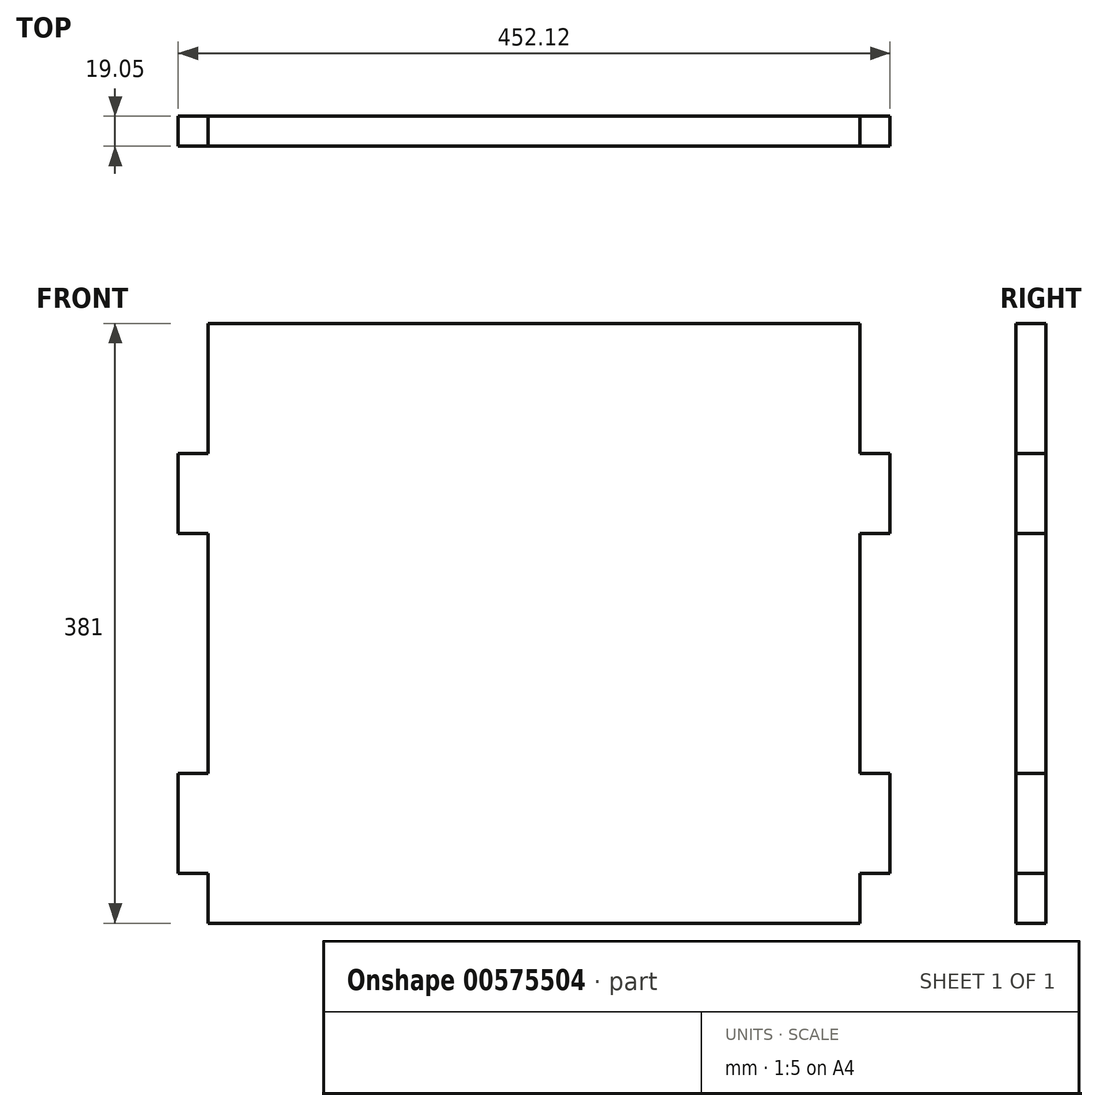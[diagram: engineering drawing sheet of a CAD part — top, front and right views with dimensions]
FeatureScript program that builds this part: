
annotation { "Feature Type Name" : "Feature", "Feature Type Description" : "" }
export const myFeature = defineFeature(function(context is Context, id is Id, definition is map)
    precondition{}
    {
        {
            var Q0;
            Q0=qCreatedBy(makeId("Front.planeOp"),FACE);
            var sketch = newSketch(context, id + "F0", { "sketchPlane" : qUnion([Q0])});
            skLineSegment(sketch, "E0.bottom", {"start": v(-259.22, 192.57) * mm, "end": v(154.8, 192.57) * mm});
            skLineSegment(sketch, "E0.top", {"start": v(-259.22, -188.43) * mm, "end": v(154.8, -188.43) * mm});
            skLineSegment(sketch, "E0.left", {"start": v(-259.22, 192.57) * mm, "end": v(-259.22, -188.43) * mm});
            skLineSegment(sketch, "E0.right", {"start": v(154.8, 192.57) * mm, "end": v(154.8, -188.43) * mm});
            skLineSegment(sketch, "E1", {"start": v(-259.22, -188.43) * mm, "end": v(-259.22, -156.68) * mm});
            skLineSegment(sketch, "E2.bottom", {"start": v(-259.22, -156.68) * mm, "end": v(-278.27, -156.68) * mm});
            skLineSegment(sketch, "E2.top", {"start": v(-259.22, -93.18) * mm, "end": v(-278.27, -93.18) * mm});
            skLineSegment(sketch, "E2.left", {"start": v(-259.22, -156.68) * mm, "end": v(-259.22, -93.18) * mm});
            skLineSegment(sketch, "E2.right", {"start": v(-278.27, -156.68) * mm, "end": v(-278.27, -93.18) * mm});
            skLineSegment(sketch, "E3", {"start": v(-278.27, -93.18) * mm, "end": v(-278.27, 59.22) * mm});
            skLineSegment(sketch, "E4.bottom", {"start": v(-278.27, 59.22) * mm, "end": v(-259.22, 59.22) * mm});
            skLineSegment(sketch, "E4.top", {"start": v(-278.27, 110.02) * mm, "end": v(-259.22, 110.02) * mm});
            skLineSegment(sketch, "E4.left", {"start": v(-278.27, 59.22) * mm, "end": v(-278.27, 110.02) * mm});
            skLineSegment(sketch, "E4.right", {"start": v(-259.22, 59.22) * mm, "end": v(-259.22, 110.02) * mm});
            skLineSegment(sketch, "E5", {"start": v(-259.22, 192.57) * mm, "end": v(-52.2, 192.57) * mm});
            skLineSegment(sketch, "E6", {"start": v(-52.2, 192.57) * mm, "end": v(-52.2, 169.4) * mm});
            skLineSegment(sketch, "E7.MirrorCS", {"start": v(154.8, -93.18) * mm, "end": v(173.85, -93.18) * mm});
            skLineSegment(sketch, "E8.MirrorCS", {"start": v(154.8, -156.68) * mm, "end": v(173.85, -156.68) * mm});
            skLineSegment(sketch, "E9.MirrorCS", {"start": v(173.85, 110.02) * mm, "end": v(154.8, 110.02) * mm});
            skLineSegment(sketch, "E10.MirrorCS", {"start": v(173.85, 59.22) * mm, "end": v(154.8, 59.22) * mm});
            skLineSegment(sketch, "E11.MirrorCS", {"start": v(173.85, -156.68) * mm, "end": v(173.85, -93.18) * mm});
            skLineSegment(sketch, "E12.MirrorCS", {"start": v(154.8, -156.68) * mm, "end": v(154.8, -93.18) * mm});
            skLineSegment(sketch, "E13.MirrorCS", {"start": v(173.85, 59.22) * mm, "end": v(173.85, 110.02) * mm});
            skLineSegment(sketch, "E14.MirrorCS", {"start": v(154.8, -188.43) * mm, "end": v(154.8, -156.68) * mm});
            skLineSegment(sketch, "E15.MirrorCS", {"start": v(173.85, -93.18) * mm, "end": v(173.85, 59.22) * mm});
            skLineSegment(sketch, "E16.MirrorCS", {"start": v(154.8, 59.22) * mm, "end": v(154.8, 110.02) * mm});
            skSolve(sketch);
        }
        {
            var Q0;
            Q0=makeQuery(id+"F0.imprint","IMPRINT",FACE,{"disambiguationData":[TD([[makeQuery(id+"F0.imprint","IMPRINT",EDGE,{"derivedFrom":sQuery(id+"F0.wireOp",EDGE,"E2.bottom")}),-1.0]])]});
            var Q1;
            Q1=makeQuery(id+"F0.imprint","IMPRINT",FACE,{"disambiguationData":[TD([[makeQuery(id+"F0.imprint","IMPRINT",EDGE,{"derivedFrom":sQuery(id+"F0.wireOp",EDGE,"E4.bottom")}),1.0]])]});
            var Q2;
            Q2=makeQuery(id+"F0.imprint","IMPRINT",FACE,{"disambiguationData":[TD([[makeQuery(id+"F0.imprint","IMPRINT",EDGE,{"derivedFrom":sQuery(id+"F0.wireOp",EDGE,"E7.MirrorCS")}),-1.0]])]});
            var Q3;
            Q3=makeQuery(id+"F0.imprint","IMPRINT",FACE,{"disambiguationData":[TD([[makeQuery(id+"F0.imprint","IMPRINT",EDGE,{"derivedFrom":sQuery(id+"F0.wireOp",EDGE,"E9.MirrorCS")}),1.0]])]});
            var Q4;
            {var subQ6=sQuery(id+"F0.wireOp",EDGE,"E0.bottom");Q4=makeQuery(id+"F0.imprint","IMPRINT",FACE,{"disambiguationData":[TD([[makeQuery(id+"F0.imprint","IMPRINT",EDGE,{"derivedFrom":subQ6}),-1.0]])]});}
            extrude(context, id + "F1", {"entities" : qUnion([Q0, Q1, Q2, Q3, Q4]), "depth" : 19.05 * mm, "offsetDistance" : 25.4 * mm});
        }
    });
